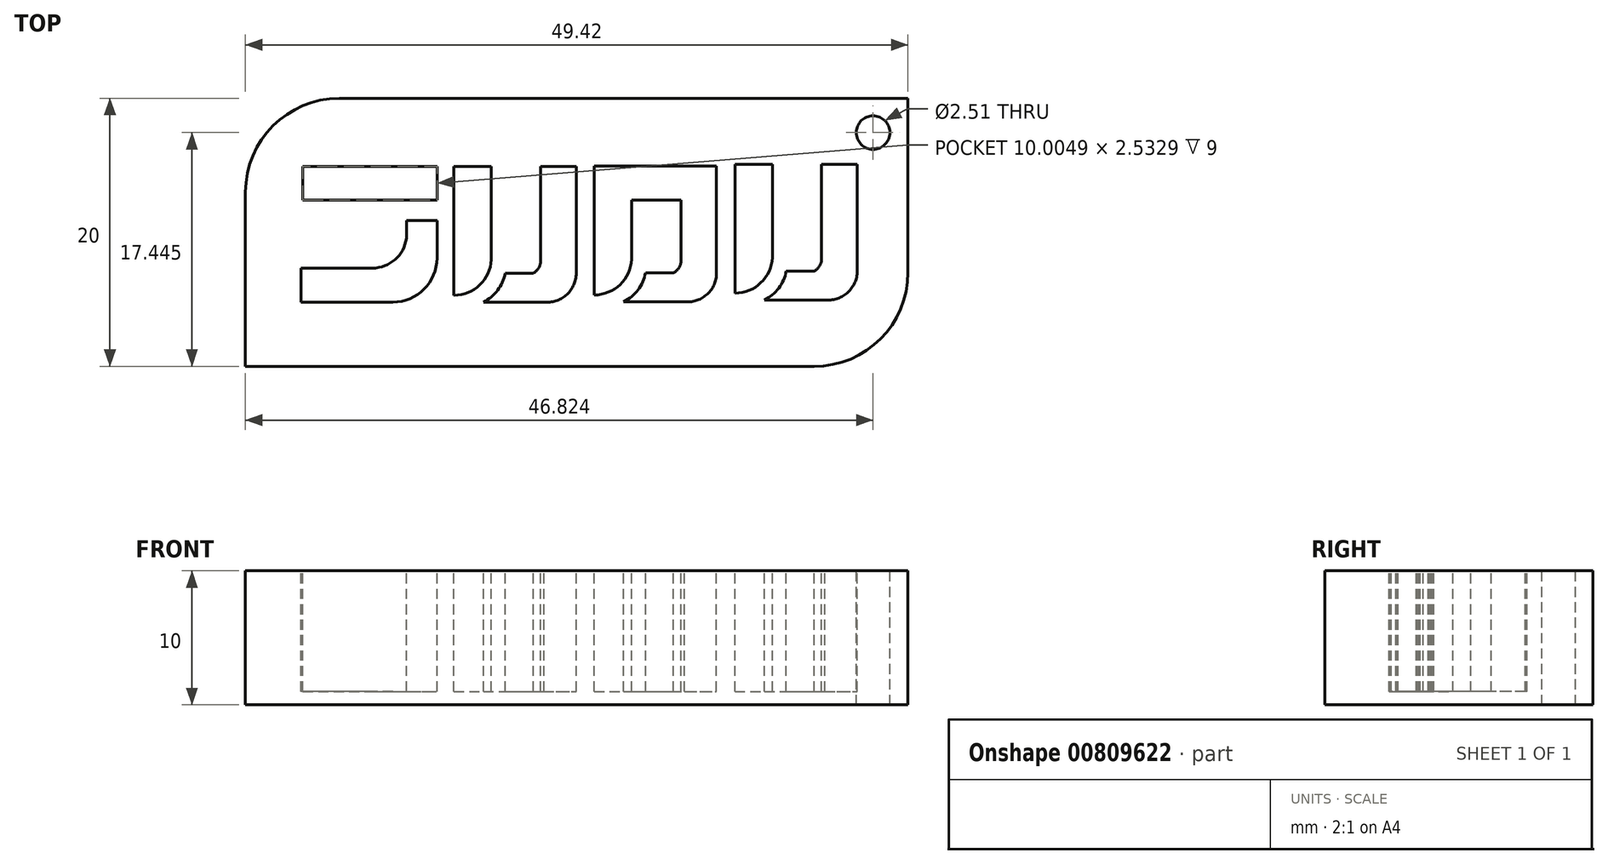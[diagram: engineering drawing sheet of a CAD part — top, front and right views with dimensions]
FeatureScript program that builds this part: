
annotation { "Feature Type Name" : "Feature", "Feature Type Description" : "" }
export const myFeature = defineFeature(function(context is Context, id is Id, definition is map)
    precondition{}
    {
        {
            var Q0;
            Q0=qCreatedBy(makeId("Top.planeOp"),FACE);
            var sketch = newSketch(context, id + "F0", { "sketchPlane" : qUnion([Q0])});
            skLineSegment(sketch, "E0.bottom", {"start": v(-24.71, 10) * mm, "end": v(24.71, 10) * mm});
            skLineSegment(sketch, "E0.top", {"start": v(-24.71, -10) * mm, "end": v(24.71, -10) * mm});
            skLineSegment(sketch, "E0.left", {"start": v(-24.71, 10) * mm, "end": v(-24.71, -10) * mm});
            skLineSegment(sketch, "E0.right", {"start": v(24.71, 10) * mm, "end": v(24.71, -10) * mm});
            skPoint(sketch, "E0.middle", {"position": v(0, 0) * mm});
            skSolve(sketch);
        }
        {
            var Q0;
            Q0 = qSketchRegion(id + "F0", true);
            extrude(context, id + "F1", {"entities" : qUnion([Q0]), "depth" : 10 * mm, "offsetDistance" : 25 * mm});
        }
        {
            var Q0;
            Q0=makeQuery(id+"F1.opExtrude","CAP_FACE",FACE,{"disambiguationData":[OSD([sQuery(id+"F0.wireOp",EDGE,"E0.bottom"),sQuery(id+"F0.wireOp",EDGE,"E0.top"),sQuery(id+"F0.wireOp",EDGE,"E0.left"),sQuery(id+"F0.wireOp",EDGE,"E0.right")])],"isStart":false});
            var sketch = newSketch(context, id + "F2", { "sketchPlane" : qUnion([Q0])});
            skLineSegment(sketch, "E1.bottom", {"start": v(-20.43, 4.93) * mm, "end": v(-10.42, 4.93) * mm});
            skLineSegment(sketch, "E1.top", {"start": v(-20.43, 2.4) * mm, "end": v(-10.42, 2.4) * mm});
            skLineSegment(sketch, "E1.left", {"start": v(-20.43, 4.93) * mm, "end": v(-20.43, 2.4) * mm});
            skLineSegment(sketch, "E1.right", {"start": v(-10.42, 4.93) * mm, "end": v(-10.42, 2.4) * mm});
            skLineSegment(sketch, "E2.bottom", {"start": v(-12.7, 0.88) * mm, "end": v(-10.42, 0.88) * mm});
            skLineSegment(sketch, "E2.left", {"start": v(-12.7, 0.88) * mm, "end": v(-12.7, -0.44) * mm});
            skLineSegment(sketch, "E2.right", {"start": v(-10.42, 0.88) * mm, "end": v(-10.42, -1.9) * mm});
            skLineSegment(sketch, "E3.bottom", {"start": v(-15.23, -2.67) * mm, "end": v(-20.55, -2.67) * mm});
            skLineSegment(sketch, "E3.top", {"start": v(-13.72, -5.2) * mm, "end": v(-20.55, -5.2) * mm});
            skLineSegment(sketch, "E3.right", {"start": v(-20.55, -2.67) * mm, "end": v(-20.55, -5.2) * mm});
            skArc(sketch, "E4", {"start": v(-13.72, -5.2) * mm, "mid": v(-11.39, -4.24) * mm, "end": v(-10.42, -1.9) * mm});
            skArc(sketch, "E5", {"start": v(-15.23, -2.67) * mm, "mid": v(-13.3, -1.78) * mm, "end": v(-12.7, 0.25) * mm});
            skLineSegment(sketch, "E6.bottom", {"start": v(-9.16, 4.93) * mm, "end": v(-6.37, 4.93) * mm});
            skLineSegment(sketch, "E6.left", {"start": v(-9.16, 4.93) * mm, "end": v(-9.16, -4.7) * mm});
            skLineSegment(sketch, "E6.right", {"start": v(-6.37, 4.93) * mm, "end": v(-6.37, -2.03) * mm});
            skArc(sketch, "E7", {"start": v(-9.16, -4.7) * mm, "mid": v(-7.23, -3.92) * mm, "end": v(-6.37, -2.03) * mm});
            skLineSegment(sketch, "E8.bottom", {"start": v(-2.7, 4.93) * mm, "end": v(-0.04, 4.93) * mm});
            skLineSegment(sketch, "E8.left", {"start": v(-2.7, 4.93) * mm, "end": v(-2.7, -2.29) * mm});
            skLineSegment(sketch, "E8.right", {"start": v(-0.04, 4.93) * mm, "end": v(-0.04, -3.17) * mm});
            skLineSegment(sketch, "E9.bottom", {"start": v(-6.37, -5.2) * mm, "end": v(-2.44, -5.2) * mm});
            skLineSegment(sketch, "E9.top", {"start": v(-5.33, -3.04) * mm, "end": v(-3.24, -3.04) * mm});
            skArc(sketch, "E10", {"start": v(-2.44, -5.2) * mm, "mid": v(-0.8, -4.7) * mm, "end": v(-0.04, -3.17) * mm});
            skArc(sketch, "E11", {"start": v(-4.28, -3.04) * mm, "mid": v(-3.13, -2.97) * mm, "end": v(-2.7, -1.9) * mm});
            skArc(sketch, "E12", {"start": v(-6.96, -5.2) * mm, "mid": v(-5.89, -4.31) * mm, "end": v(-5.33, -3.04) * mm});
            skLineSegment(sketch, "E13", {"start": v(-6.96, -5.2) * mm, "end": v(-6.37, -5.2) * mm});
            skPoint(sketch, "E9.right.end.orphan", {"position": v(-0.04, -3.04) * mm});
            skLineSegment(sketch, "E14.bottom", {"start": v(1.31, 4.95) * mm, "end": v(4.1, 4.95) * mm});
            skLineSegment(sketch, "E14.left", {"start": v(1.31, 4.95) * mm, "end": v(1.31, -4.67) * mm});
            skLineSegment(sketch, "E14.right", {"start": v(4.1, 2.4) * mm, "end": v(4.1, -2.01) * mm});
            skArc(sketch, "E15", {"start": v(1.31, -4.67) * mm, "mid": v(3.24, -3.9) * mm, "end": v(4.1, -2.01) * mm});
            skLineSegment(sketch, "E16.bottom", {"start": v(7.77, 4.95) * mm, "end": v(10.43, 4.95) * mm});
            skLineSegment(sketch, "E16.left", {"start": v(7.77, 2.4) * mm, "end": v(7.77, -2.26) * mm});
            skLineSegment(sketch, "E16.right", {"start": v(10.43, 4.95) * mm, "end": v(10.43, -3.15) * mm});
            skLineSegment(sketch, "E17.bottom", {"start": v(4.1, -5.18) * mm, "end": v(8.02, -5.18) * mm});
            skLineSegment(sketch, "E17.top", {"start": v(5.14, -3.02) * mm, "end": v(7.23, -3.02) * mm});
            skArc(sketch, "E18", {"start": v(8.02, -5.18) * mm, "mid": v(9.66, -4.68) * mm, "end": v(10.43, -3.15) * mm});
            skArc(sketch, "E19", {"start": v(6.2, -3.02) * mm, "mid": v(7.34, -2.95) * mm, "end": v(7.77, -1.88) * mm});
            skArc(sketch, "E20", {"start": v(3.5, -5.18) * mm, "mid": v(4.58, -4.3) * mm, "end": v(5.14, -3.02) * mm});
            skLineSegment(sketch, "E21", {"start": v(3.5, -5.18) * mm, "end": v(4.1, -5.18) * mm});
            skPoint(sketch, "E17.right.end.orphan", {"position": v(10.43, -3.02) * mm});
            skLineSegment(sketch, "E22.bottom", {"start": v(1.31, 4.95) * mm, "end": v(10.43, 4.95) * mm});
            skLineSegment(sketch, "E22.top", {"start": v(4.1, 2.4) * mm, "end": v(7.77, 2.4) * mm});
            skLineSegment(sketch, "E22.left", {"start": v(1.31, 4.95) * mm, "end": v(1.31, 2.4) * mm});
            skLineSegment(sketch, "E22.right", {"start": v(10.43, 4.95) * mm, "end": v(10.43, 2.4) * mm});
            skLineSegment(sketch, "E23.bottom", {"start": v(11.8, 5.09) * mm, "end": v(14.6, 5.09) * mm});
            skLineSegment(sketch, "E23.left", {"start": v(11.8, 5.09) * mm, "end": v(11.8, -4.54) * mm});
            skLineSegment(sketch, "E23.right", {"start": v(14.6, 5.09) * mm, "end": v(14.6, -1.88) * mm});
            skArc(sketch, "E24", {"start": v(11.8, -4.54) * mm, "mid": v(13.74, -3.77) * mm, "end": v(14.6, -1.88) * mm});
            skLineSegment(sketch, "E25.bottom", {"start": v(18.27, 5.09) * mm, "end": v(20.93, 5.09) * mm});
            skLineSegment(sketch, "E25.left", {"start": v(18.27, 5.09) * mm, "end": v(18.27, -2.13) * mm});
            skLineSegment(sketch, "E25.right", {"start": v(20.93, 5.09) * mm, "end": v(20.93, -3.02) * mm});
            skLineSegment(sketch, "E26.bottom", {"start": v(14.6, -5.04) * mm, "end": v(18.52, -5.04) * mm});
            skLineSegment(sketch, "E26.top", {"start": v(15.64, -2.89) * mm, "end": v(17.73, -2.89) * mm});
            skArc(sketch, "E27", {"start": v(18.52, -5.04) * mm, "mid": v(20.16, -4.55) * mm, "end": v(20.93, -3.02) * mm});
            skArc(sketch, "E28", {"start": v(16.69, -2.89) * mm, "mid": v(17.84, -2.82) * mm, "end": v(18.27, -1.75) * mm});
            skArc(sketch, "E29", {"start": v(14, -5.04) * mm, "mid": v(15.08, -4.16) * mm, "end": v(15.64, -2.89) * mm});
            skLineSegment(sketch, "E30", {"start": v(14, -5.04) * mm, "end": v(14.6, -5.04) * mm});
            skPoint(sketch, "E26.right.end.orphan", {"position": v(20.93, -2.89) * mm});
            skSolve(sketch);
        }
        {
            var Q0;
            Q0 = qSketchRegion(id + "F2", true);
            extrude(context, id + "F3", {"entities" : qUnion([Q0]), "operationType" : NewBodyOperationType.REMOVE, "oppositeDirection" : true, "depth" : 9 * mm, "offsetDistance" : 25 * mm});
        }
        {
            var Q0;
            Q0=makeQuery(id+"F1.opExtrude","SWEPT_EDGE",EDGE,{"disambiguationData":[OSD([sQuery(id+"F0.wireOp",EDGE,"E0.bottom"),sQuery(id+"F0.wireOp",EDGE,"E0.left")])]});
            var Q1;
            Q1=makeQuery(id+"F1.opExtrude","SWEPT_EDGE",EDGE,{"disambiguationData":[OSD([sQuery(id+"F0.wireOp",EDGE,"E0.top"),sQuery(id+"F0.wireOp",EDGE,"E0.right")])]});
            fillet(context, id + "F4", {"entities" : qUnion([Q0, Q1]), "radius" : 7 * mm, "tangentPropagation" : true, "allowEdgeOverflow" : false});
        }
        {
            var Q0;
            Q0=makeQuery(id+"F1.opExtrude","CAP_FACE",FACE,{"disambiguationData":[OSD([sQuery(id+"F0.wireOp",EDGE,"E0.bottom"),sQuery(id+"F0.wireOp",EDGE,"E0.top"),sQuery(id+"F0.wireOp",EDGE,"E0.left"),sQuery(id+"F0.wireOp",EDGE,"E0.right")])],"isStart":false});
            var sketch = newSketch(context, id + "F5", { "sketchPlane" : qUnion([Q0])});
            skCircle(sketch, "E31", {"center": v(22.11, 7.45) * mm, "radius": 1.25 * mm});
            skSolve(sketch);
        }
        {
            var Q0;
            Q0 = qSketchRegion(id + "F5", true);
            extrude(context, id + "F6", {"entities" : qUnion([Q0]), "operationType" : NewBodyOperationType.REMOVE, "endBound" : BoundingType.THROUGH_ALL, "oppositeDirection" : true, "depth" : 25 * mm, "offsetDistance" : 25 * mm});
        }
    });
